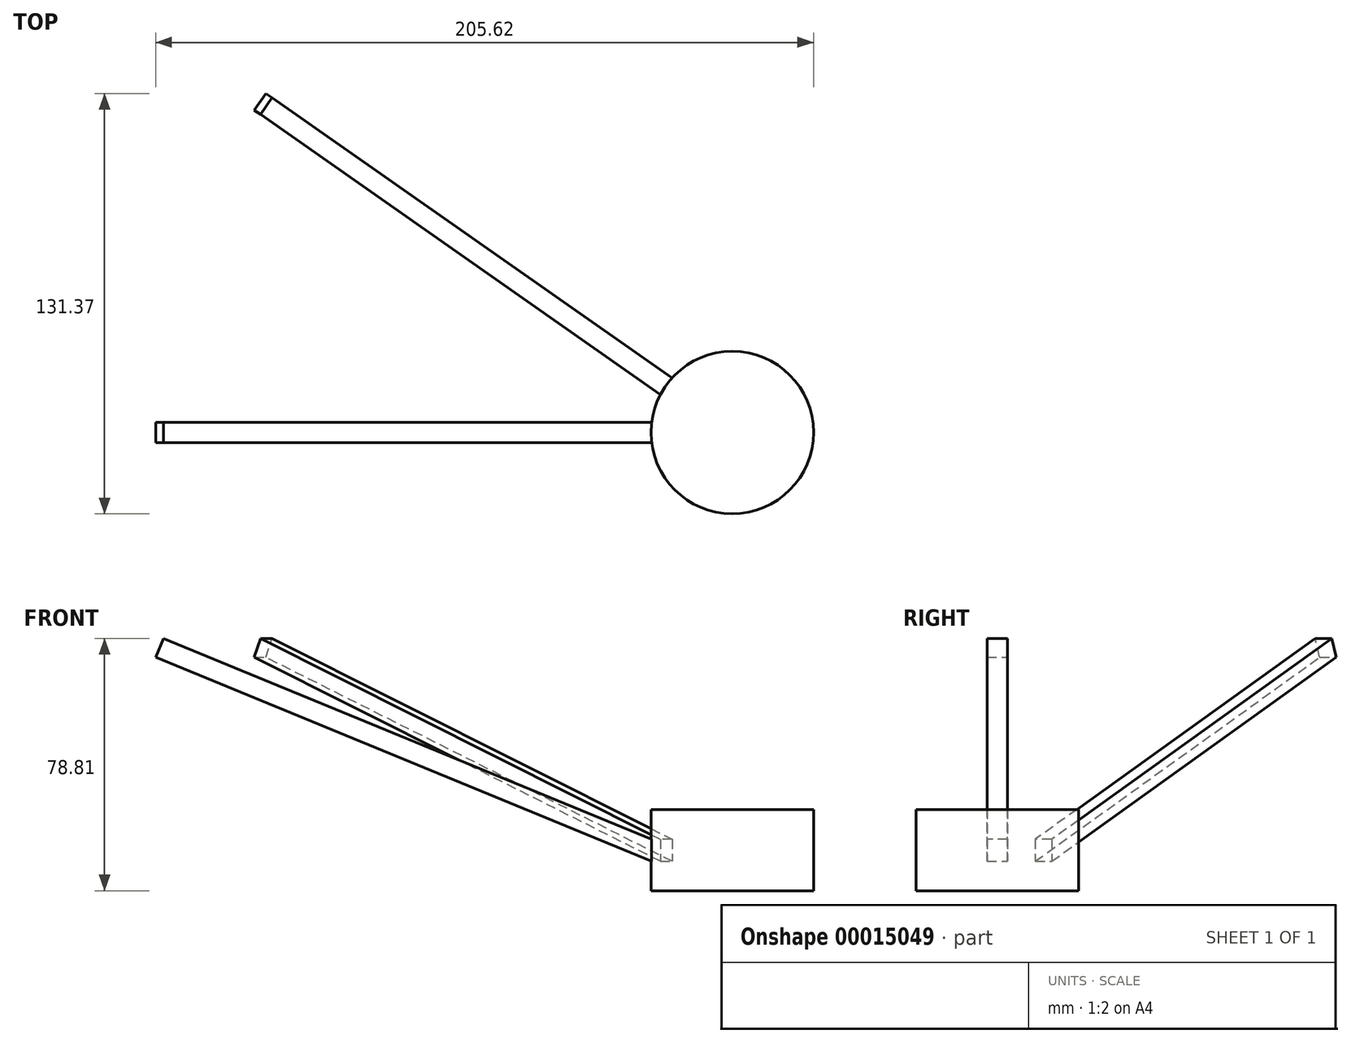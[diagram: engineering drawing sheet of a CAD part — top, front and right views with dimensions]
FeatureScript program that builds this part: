
annotation { "Feature Type Name" : "Feature", "Feature Type Description" : "" }
export const myFeature = defineFeature(function(context is Context, id is Id, definition is map)
    precondition{}
    {
        {
            var Q0;
            Q0=qCreatedBy(makeId("Top.planeOp"),FACE);
            var sketch = newSketch(context, id + "F0", { "sketchPlane" : qUnion([Q0])});
            skCircle(sketch, "E0", {"center": v(0, 0) * mm, "radius": 25.4 * mm});
            skSolve(sketch);
        }
        {
            var Q0;
            Q0 = qSketchRegion(id + "F0", true);
            extrude(context, id + "F1", {"entities" : qUnion([Q0]), "endBound" : BoundingType.SYMMETRIC, "depth" : 25.4 * mm});
        }
        {
            var Q0;
            Q0=qCreatedBy(makeId("Front.planeOp"),FACE);
            var sketch = newSketch(context, id + "F2", { "sketchPlane" : qUnion([Q0])});
            skLineSegment(sketch, "E1", {"start": v(-25.4, -3.43) * mm, "end": v(-180.22, 60.23) * mm});
            skLineSegment(sketch, "E2", {"start": v(-180.22, 60.23) * mm, "end": v(-177.8, 66.1) * mm});
            skLineSegment(sketch, "E3", {"start": v(-177.8, 66.1) * mm, "end": v(-25.4, 3.43) * mm});
            skLineSegment(sketch, "E4", {"start": v(-25.4, 12.7) * mm, "end": v(-25.4, 3.43) * mm, "construction": true});
            skLineSegment(sketch, "E5", {"start": v(-25.4, 3.43) * mm, "end": v(-16.93, -0.05) * mm});
            skLineSegment(sketch, "E6", {"start": v(-16.93, -0.05) * mm, "end": v(-19.35, -5.92) * mm});
            skLineSegment(sketch, "E7", {"start": v(-19.35, -5.92) * mm, "end": v(-25.4, -3.43) * mm});
            skLineSegment(sketch, "E8", {"start": v(-25.4, -12.7) * mm, "end": v(-25.4, -3.43) * mm, "construction": true});
            skLineSegment(sketch, "E9", {"start": v(-25.4, 3.43) * mm, "end": v(-16.93, 3.43) * mm, "construction": true});
            skLineSegment(sketch, "E10", {"start": v(-16.93, 3.43) * mm, "end": v(-8.47, 3.43) * mm, "construction": true});
            skLineSegment(sketch, "E11", {"start": v(-8.47, 3.43) * mm, "end": v(0, 3.43) * mm, "construction": true});
            skSolve(sketch);
        }
        {
            var Q0;
            Q0 = qSketchRegion(id + "F2", true);
            extrude(context, id + "F3", {"entities" : qUnion([Q0]), "operationType" : NewBodyOperationType.ADD, "endBound" : BoundingType.SYMMETRIC, "depth" : 6.35 * mm});
        }
        {
            var Q0;
            Q0=makeQuery(id+"F3.opExtrude","SWEPT_FACE",FACE,{"disambiguationData":[OSD([sQuery(id+"F2.wireOp",EDGE,"E3"),sQuery(id+"F2.wireOp",EDGE,"E5")])]});
            var Q1;
            Q1=makeQuery(id+"F3.opExtrude","CAP_FACE",FACE,{"disambiguationData":[OSD([sQuery(id+"F2.wireOp",EDGE,"E1"),sQuery(id+"F2.wireOp",EDGE,"E2"),sQuery(id+"F2.wireOp",EDGE,"E3"),sQuery(id+"F2.wireOp",EDGE,"E5"),sQuery(id+"F2.wireOp",EDGE,"E6"),sQuery(id+"F2.wireOp",EDGE,"E7")])],"isStart":false});
            var Q2;
            Q2=makeQuery(id+"F3.opExtrude","SWEPT_FACE",FACE,{"disambiguationData":[OSD([sQuery(id+"F2.wireOp",EDGE,"E2")])]});
            var Q3;
            Q3=makeQuery(id+"F3.opExtrude","SWEPT_FACE",FACE,{"disambiguationData":[OSD([sQuery(id+"F2.wireOp",EDGE,"E1"),sQuery(id+"F2.wireOp",EDGE,"E7")])]});
            var Q4;
            Q4=makeQuery(id+"F3.opExtrude","CAP_FACE",FACE,{"disambiguationData":[OSD([sQuery(id+"F2.wireOp",EDGE,"E1"),sQuery(id+"F2.wireOp",EDGE,"E2"),sQuery(id+"F2.wireOp",EDGE,"E3"),sQuery(id+"F2.wireOp",EDGE,"E5"),sQuery(id+"F2.wireOp",EDGE,"E6"),sQuery(id+"F2.wireOp",EDGE,"E7")])],"isStart":true});
            var Q5;
            Q5=makeQuery(id+"F1.opExtrude","SWEPT_FACE",FACE,{"disambiguationData":[OSD([sQuery(id+"F0.wireOp",EDGE,"E0")])]});
            circularPattern(context, id + "F4", {"faces" : qUnion([Q0, Q1, Q2, Q3, Q4]), "axis" : qUnion([Q5]), "angle" : 35 * degree, "instanceCount" : 2, "patternType" : PatternType.FACE});
        }
    });
